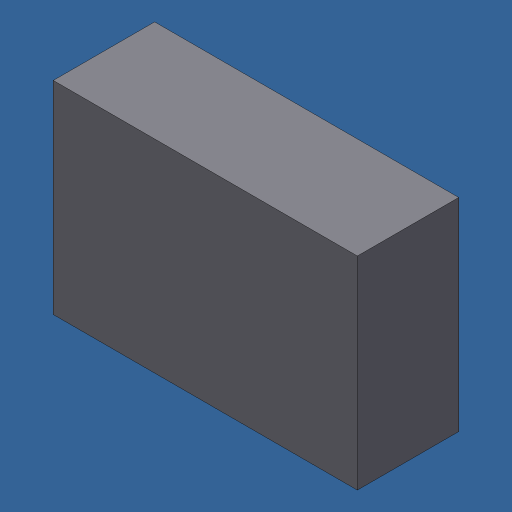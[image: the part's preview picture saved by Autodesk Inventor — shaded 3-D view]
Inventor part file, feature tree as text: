
AUTODESK INVENTOR PART (.ipt)
format: ipt  version: 2024.3 (Build 283343000, 343)  size: 109,568 bytes
history: native  units: mm (DEFAULTED — no unit token found)
features: other x1, extrude x1
ambient origin geometry x8: Origin, YZ Plane, XZ Plane, XY Plane, X Axis, Y Axis, Z Axis, Center Point
bodies: Body1 (feature_tree)
feature tree (2):
  other  "Finish - None"
  extrude  "Extrusion1"  TaperAngle=0.0deg  [1 undecoded]
note: 1 required parameter value undecoded (feature->parameter linkage not recoverable at this tier; creation-order binding heuristic only, values carry confidence <= 0.55)
